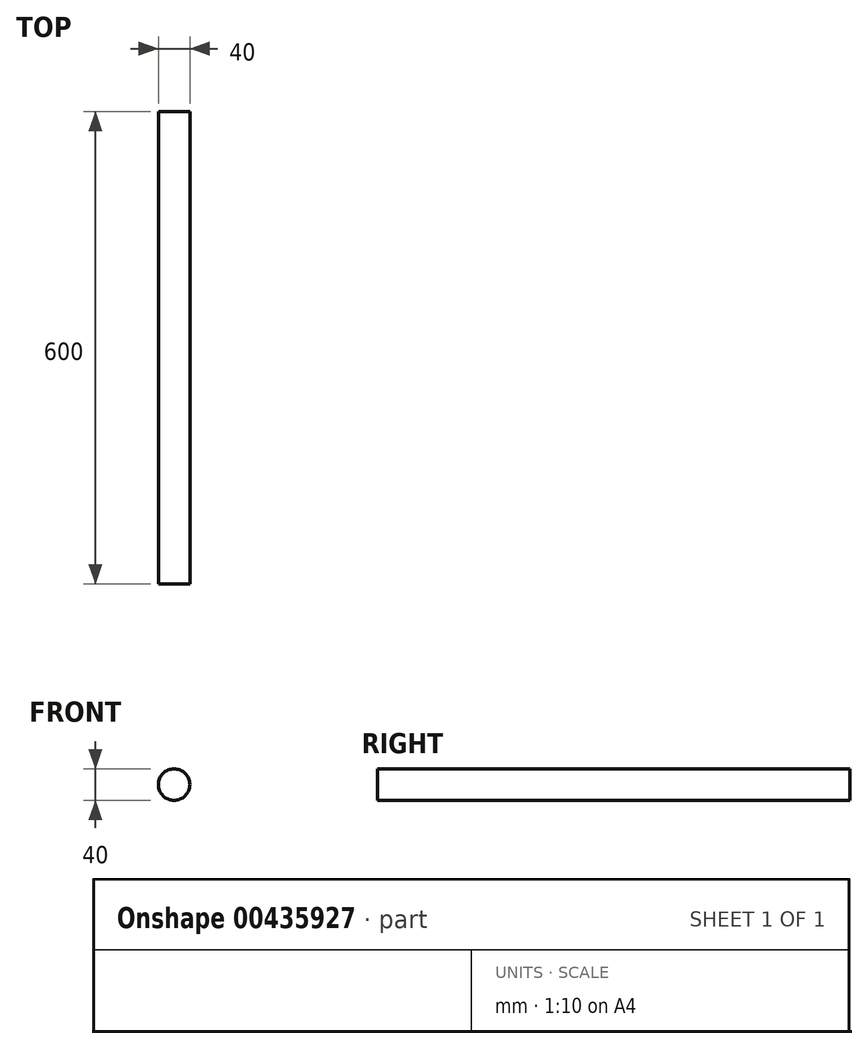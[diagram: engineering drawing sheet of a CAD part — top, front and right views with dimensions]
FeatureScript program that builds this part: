
annotation { "Feature Type Name" : "Feature", "Feature Type Description" : "" }
export const myFeature = defineFeature(function(context is Context, id is Id, definition is map)
    precondition{}
    {
        {
            var Q0;
            Q0=qCreatedBy(makeId("Front.planeOp"),FACE);
            var sketch = newSketch(context, id + "F0", { "sketchPlane" : qUnion([Q0])});
            skCircle(sketch, "E0", {"center": v(0, 0) * mm, "radius": 20 * mm});
            skSolve(sketch);
        }
        {
            var Q0;
            Q0=makeQuery(id+"F0.imprint","IMPRINT",FACE,{"disambiguationData":[TD([[makeQuery(id+"F0.imprint","IMPRINT",EDGE,{"derivedFrom":sQuery(id+"F0.wireOp",EDGE,"E0")}),1.0]])]});
            extrude(context, id + "F1", {"entities" : qUnion([Q0]), "endBound" : BoundingType.SYMMETRIC, "depth" : 600 * mm});
        }
    });
